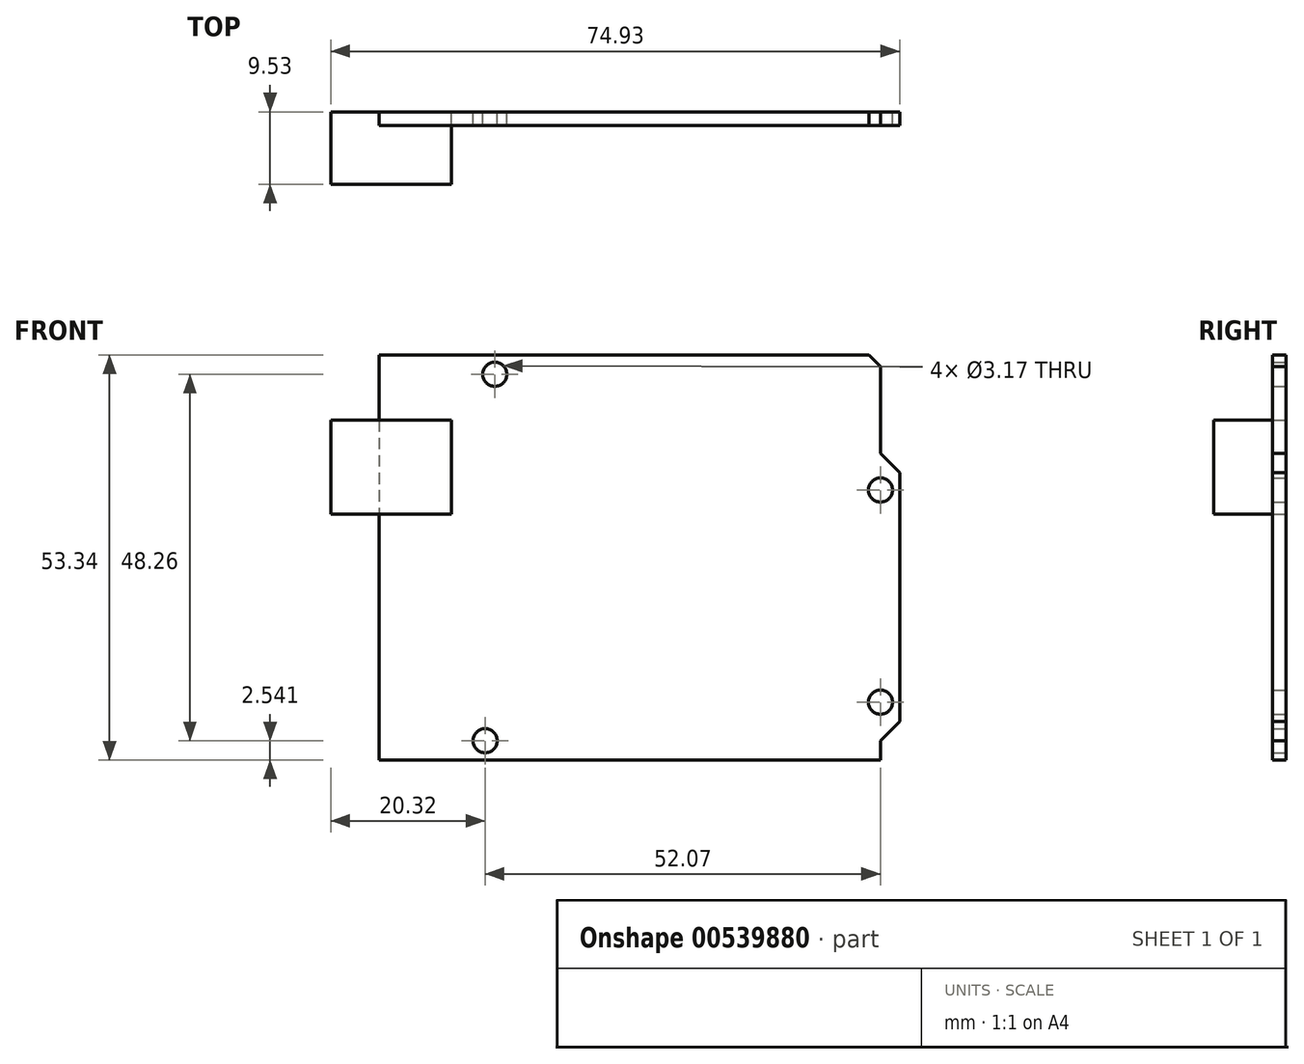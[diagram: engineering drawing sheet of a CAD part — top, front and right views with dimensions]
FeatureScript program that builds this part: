
annotation { "Feature Type Name" : "Feature", "Feature Type Description" : "" }
export const myFeature = defineFeature(function(context is Context, id is Id, definition is map)
    precondition{}
    {
        {
            var Q0;
            Q0=qCreatedBy(makeId("Front.planeOp"),FACE);
            var sketch = newSketch(context, id + "F0", { "sketchPlane" : qUnion([Q0])});
            skLineSegment(sketch, "E0", {"start": v(-50.93, 10.74) * mm, "end": v(-50.93, -42.6) * mm});
            skLineSegment(sketch, "E1", {"start": v(-50.93, 10.74) * mm, "end": v(13.59, 10.74) * mm});
            skPoint(sketch, "E2", {"position": v(15.11, 9.22) * mm});
            skLineSegment(sketch, "E3", {"start": v(15.11, 9.22) * mm, "end": v(13.59, 10.74) * mm});
            skLineSegment(sketch, "E4", {"start": v(15.11, 9.22) * mm, "end": v(15.11, -2.21) * mm});
            skPoint(sketch, "E5", {"position": v(17.65, -4.75) * mm});
            skLineSegment(sketch, "E6", {"start": v(15.11, -2.21) * mm, "end": v(17.65, -4.75) * mm});
            skLineSegment(sketch, "E7", {"start": v(17.65, -37.52) * mm, "end": v(17.65, -4.75) * mm});
            skLineSegment(sketch, "E8", {"start": v(17.65, -37.52) * mm, "end": v(15.11, -40.06) * mm});
            skLineSegment(sketch, "E9", {"start": v(-50.93, -42.6) * mm, "end": v(15.11, -42.6) * mm});
            skLineSegment(sketch, "E10", {"start": v(15.11, -42.6) * mm, "end": v(15.11, -40.06) * mm});
            skCircle(sketch, "E11", {"center": v(-36.96, -40.06) * mm, "radius": 1.59 * mm});
            skCircle(sketch, "E12", {"center": v(-35.69, 8.2) * mm, "radius": 1.59 * mm});
            skCircle(sketch, "E13", {"center": v(15.11, -7.04) * mm, "radius": 1.59 * mm});
            skCircle(sketch, "E14", {"center": v(15.11, -34.98) * mm, "radius": 1.59 * mm});
            skSolve(sketch);
        }
        {
            var Q0;
            Q0=qCreatedBy(makeId("Front.planeOp"),FACE);
            var sketch = newSketch(context, id + "F1", { "sketchPlane" : qUnion([Q0])});
            skPoint(sketch, "E15", {"position": v(-41.4, -10.21) * mm});
            skLineSegment(sketch, "E16.bottom", {"start": v(-41.4, -10.21) * mm, "end": v(-57.28, -10.21) * mm});
            skLineSegment(sketch, "E16.left", {"start": v(-41.4, -10.21) * mm, "end": v(-41.4, -10.21) * mm});
            skLineSegment(sketch, "E16.right", {"start": v(-57.28, -10.21) * mm, "end": v(-57.28, -10.21) * mm});
            skLineSegment(sketch, "E17.top", {"start": v(-57.28, 2.14) * mm, "end": v(-57.28, 2.14) * mm});
            skLineSegment(sketch, "E17.left", {"start": v(-57.28, -10.21) * mm, "end": v(-57.28, 2.14) * mm});
            skLineSegment(sketch, "E18.bottom", {"start": v(-41.4, 2.14) * mm, "end": v(-41.4, 2.14) * mm});
            skLineSegment(sketch, "E19.top", {"start": v(-41.4, 2.14) * mm, "end": v(-57.28, 2.14) * mm});
            skLineSegment(sketch, "E20", {"start": v(-41.4, 2.14) * mm, "end": v(-41.4, -10.21) * mm});
            skPoint(sketch, "E21", {"position": v(-39.5, -39.42) * mm});
            skLineSegment(sketch, "E22.bottom", {"start": v(-39.5, -39.42) * mm, "end": v(-52.83, -39.42) * mm});
            skLineSegment(sketch, "E22.top", {"start": v(-39.5, -39.42) * mm, "end": v(-52.83, -39.42) * mm});
            skLineSegment(sketch, "E22.left", {"start": v(-39.5, -39.42) * mm, "end": v(-39.5, -39.42) * mm});
            skLineSegment(sketch, "E22.right", {"start": v(-52.83, -39.42) * mm, "end": v(-52.83, -39.42) * mm});
            skLineSegment(sketch, "E23", {"start": v(-52.83, -39.42) * mm, "end": v(-52.83, -30.53) * mm});
            skLineSegment(sketch, "E24", {"start": v(-52.83, -30.53) * mm, "end": v(-39.5, -30.53) * mm});
            skLineSegment(sketch, "E25", {"start": v(-39.5, -30.53) * mm, "end": v(-39.5, -39.42) * mm});
            skSolve(sketch);
        }
        {
            var Q0;
            Q0=makeQuery(id+"F1.imprint","IMPRINT",FACE,{"disambiguationData":[TD([[makeQuery(id+"F1.imprint","IMPRINT",EDGE,{"derivedFrom":sQuery(id+"F1.wireOp",EDGE,"E16.bottom")}),-1.0]])]});
            var Q1;
            Q1=makeQuery(id+"F1.imprint","IMPRINT",FACE,{"disambiguationData":[TD([[makeQuery(id+"F1.imprint","IMPRINT",EDGE,{"derivedFrom":sQuery(id+"F1.wireOp",EDGE,"E22.top")}),-1.0]])]});
            extrude(context, id + "F2", {"entities" : qUnion([Q0, Q1]), "depth" : 9.52 * mm, "offsetDistance" : 25.4 * mm});
        }
        {
            var Q0;
            Q0=makeQuery(id+"F0.imprint","IMPRINT",FACE,{"disambiguationData":[TD([[makeQuery(id+"F0.imprint","IMPRINT",EDGE,{"derivedFrom":sQuery(id+"F0.wireOp",EDGE,"E0")}),1.0]])]});
            extrude(context, id + "F3", {"entities" : qUnion([Q0]), "depth" : 1.78 * mm, "offsetDistance" : 25.4 * mm});
        }
    });
